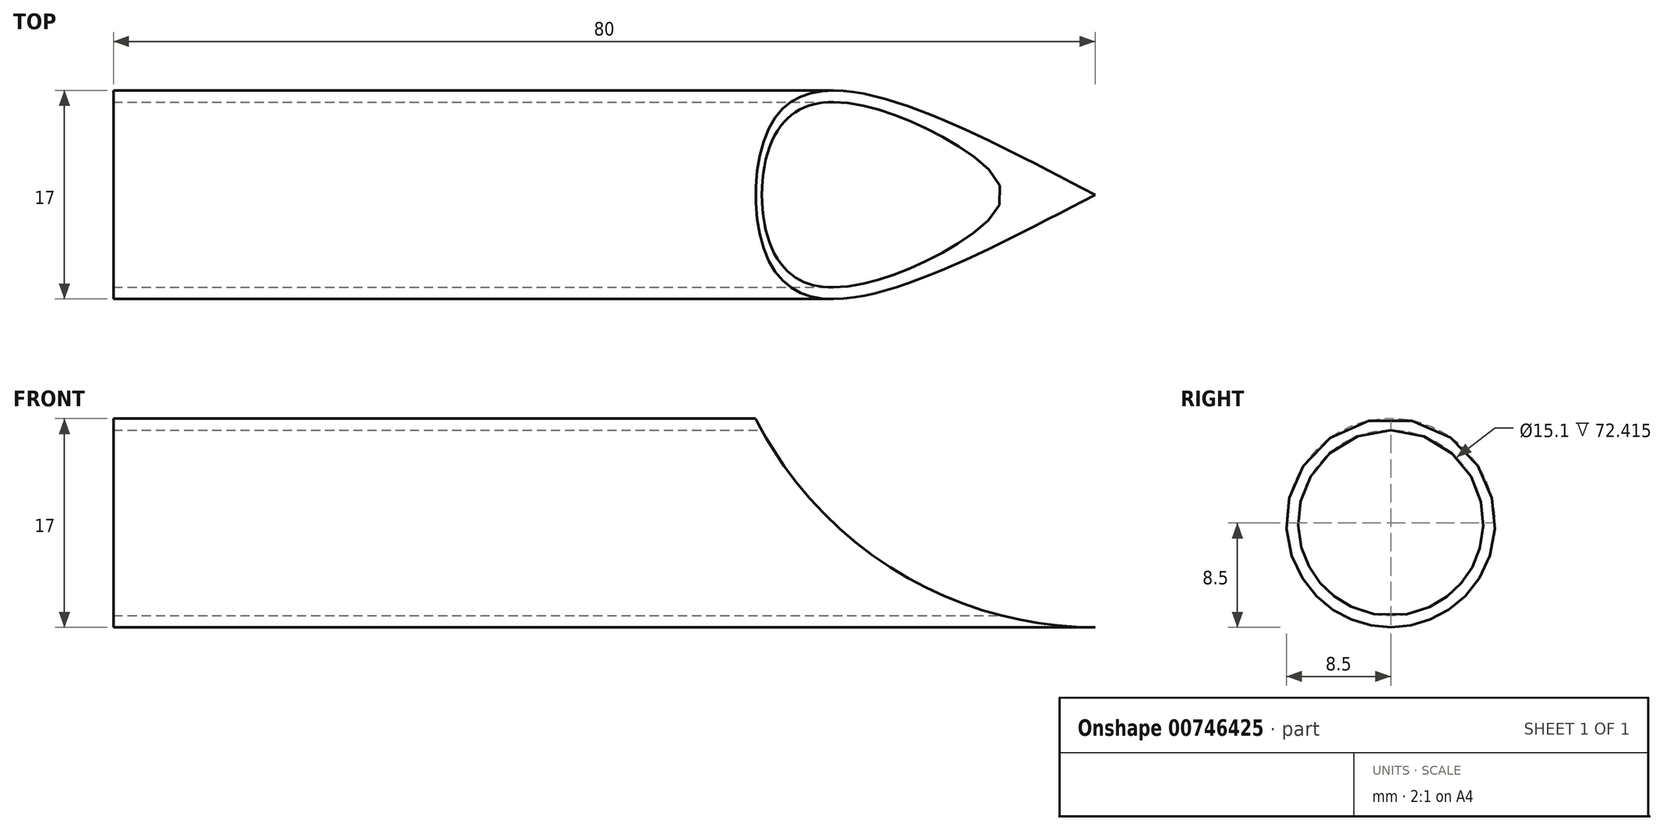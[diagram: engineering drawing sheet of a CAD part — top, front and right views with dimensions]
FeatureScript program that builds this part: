
annotation { "Feature Type Name" : "Feature", "Feature Type Description" : "" }
export const myFeature = defineFeature(function(context is Context, id is Id, definition is map)
    precondition{}
    {
        {
            var Q0;
            Q0=qCreatedBy(makeId("Top.planeOp"),FACE);
            var sketch = newSketch(context, id + "F0", { "sketchPlane" : qUnion([Q0])});
            skCircle(sketch, "E0", {"center": v(0, 0) * mm, "radius": 7.55 * mm});
            skCircle(sketch, "E1", {"center": v(0, 0) * mm, "radius": 8.5 * mm});
            skSolve(sketch);
        }
        {
            var Q0;
            Q0 = qSketchRegion(id + "F0", true);
            extrude(context, id + "F1", {"entities" : qUnion([Q0]), "depth" : 80 * mm, "offsetDistance" : 25.4 * mm});
        }
        {
            var Q0;
            Q0=qCreatedBy(makeId("Right.planeOp"),FACE);
            var sketch = newSketch(context, id + "F2", { "sketchPlane" : qUnion([Q0])});
            skPoint(sketch, "E2", {"position": v(22.5, 0) * mm});
            skCircle(sketch, "E3", {"center": v(22.5, 0) * mm, "radius": 31 * mm});
            skSolve(sketch);
        }
        {
            var Q0;
            Q0 = qSketchRegion(id + "F2", true);
            extrude(context, id + "F3", {"entities" : qUnion([Q0]), "operationType" : NewBodyOperationType.REMOVE, "oppositeDirection" : true, "depth" : 25.4 * mm, "offsetDistance" : 25.4 * mm});
        }
        {
            var Q0;
            Q0 = qSketchRegion(id + "F2", true);
            extrude(context, id + "F4", {"entities" : qUnion([Q0]), "operationType" : NewBodyOperationType.REMOVE, "depth" : 25.4 * mm, "offsetDistance" : 25.4 * mm});
        }
        {
            var Q0;
            Q0=qCreatedBy(makeId("Front.planeOp"),FACE);
            var sketch = newSketch(context, id + "F5", { "sketchPlane" : qUnion([Q0])});
            skLineSegment(sketch, "E4", {"start": v(0, 0) * mm, "end": v(67.7, 0) * mm});
            skLineSegment(sketch, "E5", {"start": v(67.7, 0) * mm, "end": v(-39.62, 0) * mm});
            skSolve(sketch);
        }
        {
            var Q0;
            Q0=makeQuery(id+"F1.opExtrude","SWEPT_BODY",BODY,{"disambiguationData":[OSD([sQuery(id+"F0.wireOp",EDGE,"E0"),sQuery(id+"F0.wireOp",EDGE,"E1")])]});
            var Q1;
            Q1=sQuery(id+"F5.wireOp",EDGE,"E5");
            transform(context, id + "F6", {"entities" : qUnion([Q0]), "transformType" : TransformType.ROTATION, "transformAxis" : qUnion([Q1]), "angle" : 90 * degree, "oppositeDirection" : true, "makeCopy" : false});
        }
        {
            var Q0;
            Q0=qCreatedBy(makeId("Front.planeOp"),FACE);
            var sketch = newSketch(context, id + "F7", { "sketchPlane" : qUnion([Q0])});
            skLineSegment(sketch, "E6", {"start": v(0, -18.23) * mm, "end": v(0, 45.3) * mm});
            skSolve(sketch);
        }
        {
            var Q0;
            Q0=makeQuery(id+"F1.opExtrude","SWEPT_BODY",BODY,{"disambiguationData":[OSD([sQuery(id+"F0.wireOp",EDGE,"E0"),sQuery(id+"F0.wireOp",EDGE,"E1")])]});
            var Q1;
            Q1=sQuery(id+"F7.wireOp",EDGE,"E6");
            transform(context, id + "F8", {"entities" : qUnion([Q0]), "transformType" : TransformType.ROTATION, "transformAxis" : qUnion([Q1]), "angle" : 90 * degree, "oppositeDirection" : true, "makeCopy" : false});
        }
    });
